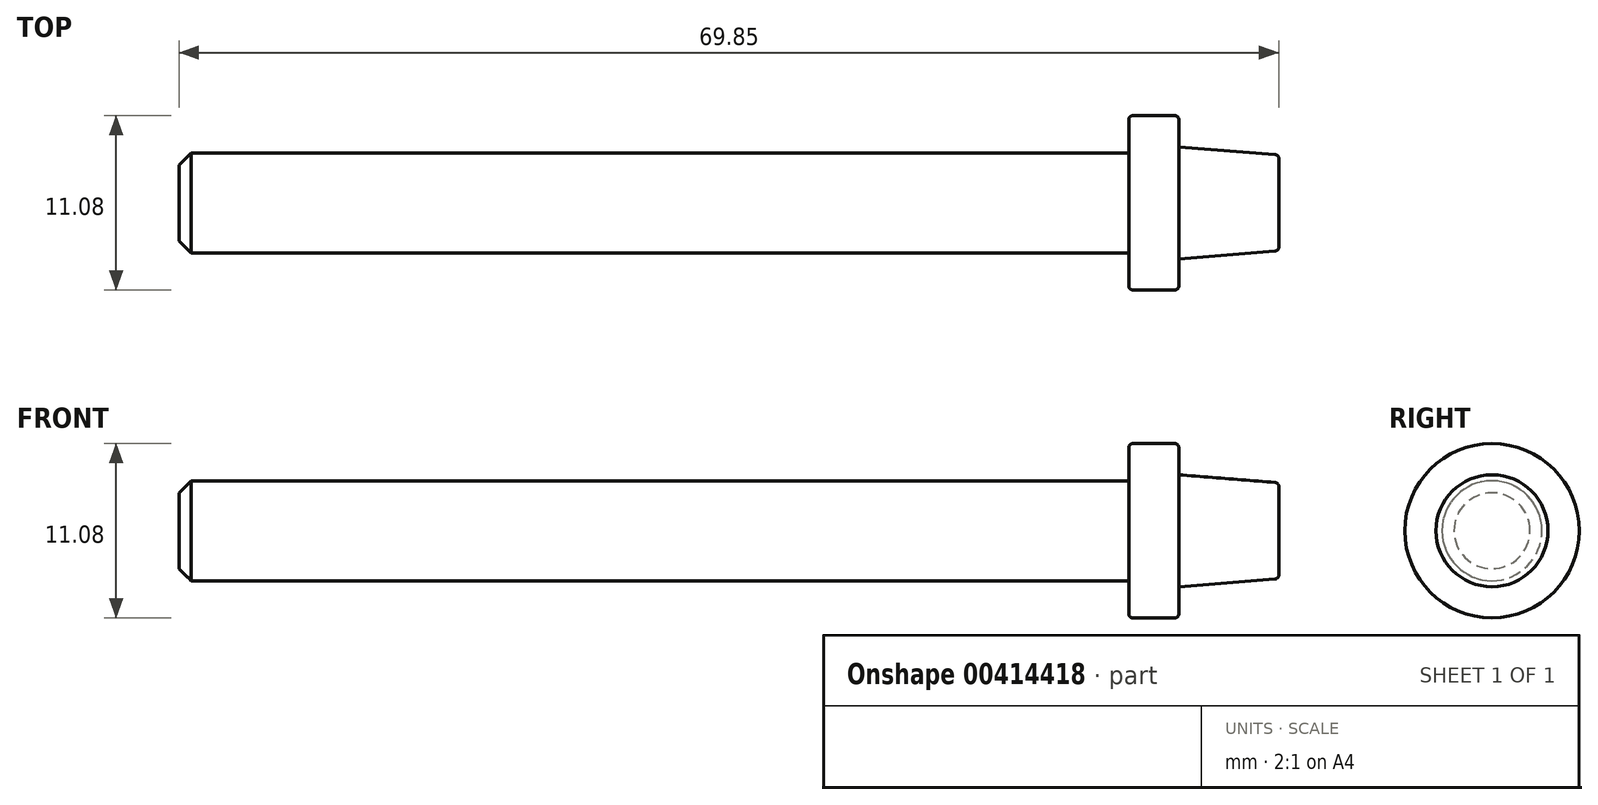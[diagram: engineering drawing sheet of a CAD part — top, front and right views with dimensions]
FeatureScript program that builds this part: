
annotation { "Feature Type Name" : "Feature", "Feature Type Description" : "" }
export const myFeature = defineFeature(function(context is Context, id is Id, definition is map)
    precondition{}
    {
        {
            var Q0;
            Q0=qCreatedBy(makeId("Top.planeOp"),FACE);
            var sketch = newSketch(context, id + "F0", { "sketchPlane" : qUnion([Q0])});
            skLineSegment(sketch, "E0", {"start": v(0, 0) * mm, "end": v(0, 3.05) * mm});
            skLineSegment(sketch, "E1", {"start": v(0, 3.05) * mm, "end": v(-6.35, 3.56) * mm});
            skLineSegment(sketch, "E2", {"start": v(-6.35, 3.56) * mm, "end": v(-6.35, 5.54) * mm});
            skLineSegment(sketch, "E3", {"start": v(-6.35, 5.54) * mm, "end": v(-9.53, 5.54) * mm});
            skLineSegment(sketch, "E4", {"start": v(-9.53, 5.54) * mm, "end": v(-9.53, 3.18) * mm});
            skLineSegment(sketch, "E5", {"start": v(-9.52, 3.18) * mm, "end": v(-69.85, 3.17) * mm});
            skLineSegment(sketch, "E6", {"start": v(-69.85, 3.17) * mm, "end": v(-69.85, 0) * mm});
            skLineSegment(sketch, "E7", {"start": v(-69.85, 0) * mm, "end": v(0, 0) * mm});
            skSolve(sketch);
        }
        {
            var Q0;
            Q0 = qSketchRegion(id + "F0", true);
            var Q1;
            Q1=sQuery(id+"F0.wireOp",EDGE,"E7");
            revolve(context, id + "F1", {"entities" : qUnion([Q0]), "axis" : qUnion([Q1]), "revolveType" : RevolveType.FULL});
        }
        {
            var Q0;
            Q0=makeQuery(id+"F1.opRevolve","SWEPT_EDGE",EDGE,{"disambiguationData":[OSD([sQuery(id+"F0.wireOp",EDGE,"E5"),sQuery(id+"F0.wireOp",EDGE,"E6")])]});
            chamfer(context, id + "F2", {"entities" : qUnion([Q0]), "width" : 0.76 * mm, "tangentPropagation" : true});
        }
        {
            var Q0;
            Q0=makeQuery(id+"F1.opRevolve","SWEPT_EDGE",EDGE,{"disambiguationData":[OSD([sQuery(id+"F0.wireOp",EDGE,"E3"),sQuery(id+"F0.wireOp",EDGE,"E4")])]});
            var Q1;
            Q1=makeQuery(id+"F1.opRevolve","SWEPT_EDGE",EDGE,{"disambiguationData":[OSD([sQuery(id+"F0.wireOp",EDGE,"E2"),sQuery(id+"F0.wireOp",EDGE,"E3")])]});
            var Q2;
            Q2=makeQuery(id+"F1.opRevolve","SWEPT_EDGE",EDGE,{"disambiguationData":[OSD([sQuery(id+"F0.wireOp",EDGE,"E0"),sQuery(id+"F0.wireOp",EDGE,"E1")])]});
            fillet(context, id + "F3", {"entities" : qUnion([Q0, Q1, Q2]), "radius" : 0.25 * mm, "tangentPropagation" : true, "allowEdgeOverflow" : false});
        }
    });
